AUTODESK INVENTOR PART (.ipt)
format: ipt  version: 2023.2 (Build 272271000, 271)  size: 92,160 bytes
history: native  units: mm
features: reference x3, other x3, plane x1, extrude x1, sketch x1
ambient origin geometry x8: Origin, YZ Plane, XZ Plane, XY Plane, X Axis, Y Axis, Z Axis, Center Point
bodies: Solid1 (feature_tree)
feature tree (9):
  plane  "Work Plane1"
  extrude  "Extrusion1"  Depth=166.999775mm
  sketch  "Sketch1"  dims[d1=5.0mm d2=0.0mm d5=20.0mm d8=20.0mm d9=180.0deg d10=160.0mm d11=90.0deg d12=166.999775mm]
  reference  "Reference1"
  reference  "Reference2"
  reference  "Reference3"
  parser-record x1  (decoder bookkeeping rows leaked as tree rows — omitted from the tree; the rows remain in map.json)
  other  "Main Assembly.iam"
  other  "V-Slot-Gantry-Plate:1"
note: 1 file-system path scrubbed to <path> (originals preserved in map.json)
